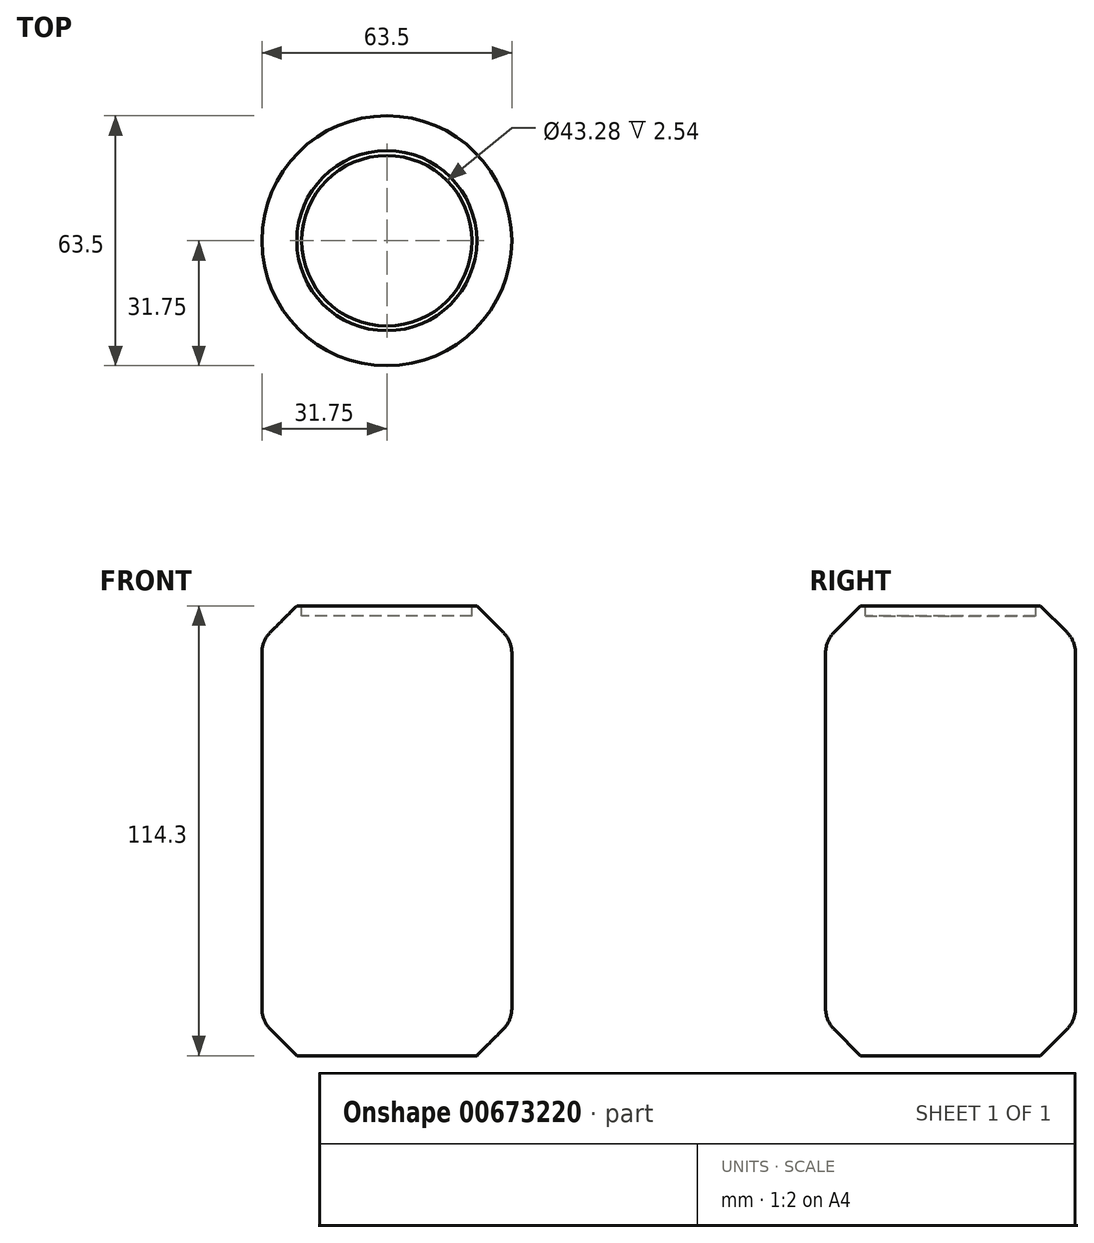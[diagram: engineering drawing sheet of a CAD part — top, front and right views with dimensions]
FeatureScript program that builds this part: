
annotation { "Feature Type Name" : "Feature", "Feature Type Description" : "" }
export const myFeature = defineFeature(function(context is Context, id is Id, definition is map)
    precondition{}
    {
        {
            var Q0;
            Q0=qCreatedBy(makeId("Top.planeOp"),FACE);
            var sketch = newSketch(context, id + "F0", { "sketchPlane" : qUnion([Q0])});
            skCircle(sketch, "E0", {"center": v(0, 0) * mm, "radius": 31.75 * mm});
            skSolve(sketch);
        }
        {
            var Q0;
            Q0 = qSketchRegion(id + "F0", true);
            extrude(context, id + "F1", {"entities" : qUnion([Q0]), "depth" : 114.3 * mm, "offsetDistance" : 25.4 * mm});
        }
        {
            var Q0;
            Q0=makeQuery(id+"F1.opExtrude","CAP_EDGE",EDGE,{"disambiguationData":[OSD([sQuery(id+"F0.wireOp",EDGE,"E0")])],"isStart":false});
            chamfer(context, id + "F2", {"entities" : qUnion([Q0]), "width" : 8.9 * mm});
        }
        {
            var Q0;
            Q0=makeQuery(id+"F1.opExtrude","CAP_EDGE",EDGE,{"disambiguationData":[OSD([sQuery(id+"F0.wireOp",EDGE,"E0")])],"isStart":true});
            chamfer(context, id + "F3", {"entities" : qUnion([Q0]), "width" : 8.9 * mm, "tangentPropagation" : true});
        }
        {
            var Q0;
            {var subQ0=sQuery(id+"F0.wireOp",EDGE,"E0");Q0=makeQuery(id+"F3.opChamfer","BLEND_EDGE",EDGE,{"blendedFrom":[makeQuery(id+"F1.opExtrude","CAP_EDGE",EDGE,{"disambiguationData":[OSD([subQ0])],"isStart":true}),makeQuery(id+"F1.opExtrude","SWEPT_FACE",FACE,{"disambiguationData":[OSD([subQ0])]})],"blendedInto":[makeQuery(id+"F1.opExtrude","SWEPT_FACE",FACE,{"disambiguationData":[OSD([subQ0])]})]});}
            var Q1;
            {var subQ0=sQuery(id+"F0.wireOp",EDGE,"E0");Q1=makeQuery(id+"F2.opChamfer","BLEND_EDGE",EDGE,{"blendedFrom":[makeQuery(id+"F1.opExtrude","CAP_EDGE",EDGE,{"disambiguationData":[OSD([subQ0])],"isStart":false}),makeQuery(id+"F1.opExtrude","SWEPT_FACE",FACE,{"disambiguationData":[OSD([subQ0])]})],"blendedInto":[makeQuery(id+"F1.opExtrude","SWEPT_FACE",FACE,{"disambiguationData":[OSD([subQ0])]})]});}
            fillet(context, id + "F4", {"entities" : qUnion([Q0, Q1]), "radius" : 7.62 * mm, "tangentPropagation" : true, "allowEdgeOverflow" : false});
        }
        {
            var Q0;
            Q0=makeQuery(id+"F1.opExtrude","CAP_FACE",FACE,{"disambiguationData":[OSD([sQuery(id+"F0.wireOp",EDGE,"E0")])],"isStart":false});
            var sketch = newSketch(context, id + "F5", { "sketchPlane" : qUnion([Q0])});
            skCircle(sketch, "E1", {"center": v(0, 0) * mm, "radius": 21.64 * mm});
            skSolve(sketch);
        }
        {
            var Q0;
            Q0 = qSketchRegion(id + "F5", true);
            var sketch = newSketch(context, id + "F6", { "sketchPlane" : qUnion([Q0])});
            skSolve(sketch);
        }
        {
            var Q0;
            Q0=makeQuery(id+"F6.imprint","IMPRINT",FACE,{"disambiguationData":[TD([[makeQuery(id+"F6.imprint","IMPRINT",EDGE,{"derivedFrom":makeQuery(id+"F5.imprint","IMPRINT",EDGE,{"derivedFrom":sQuery(id+"F5.wireOp",EDGE,"E1")})}),1.0]])]});
            extrude(context, id + "F7", {"entities" : qUnion([Q0]), "operationType" : NewBodyOperationType.REMOVE, "oppositeDirection" : true, "depth" : 2.54 * mm, "offsetDistance" : 25.4 * mm});
        }
    });
